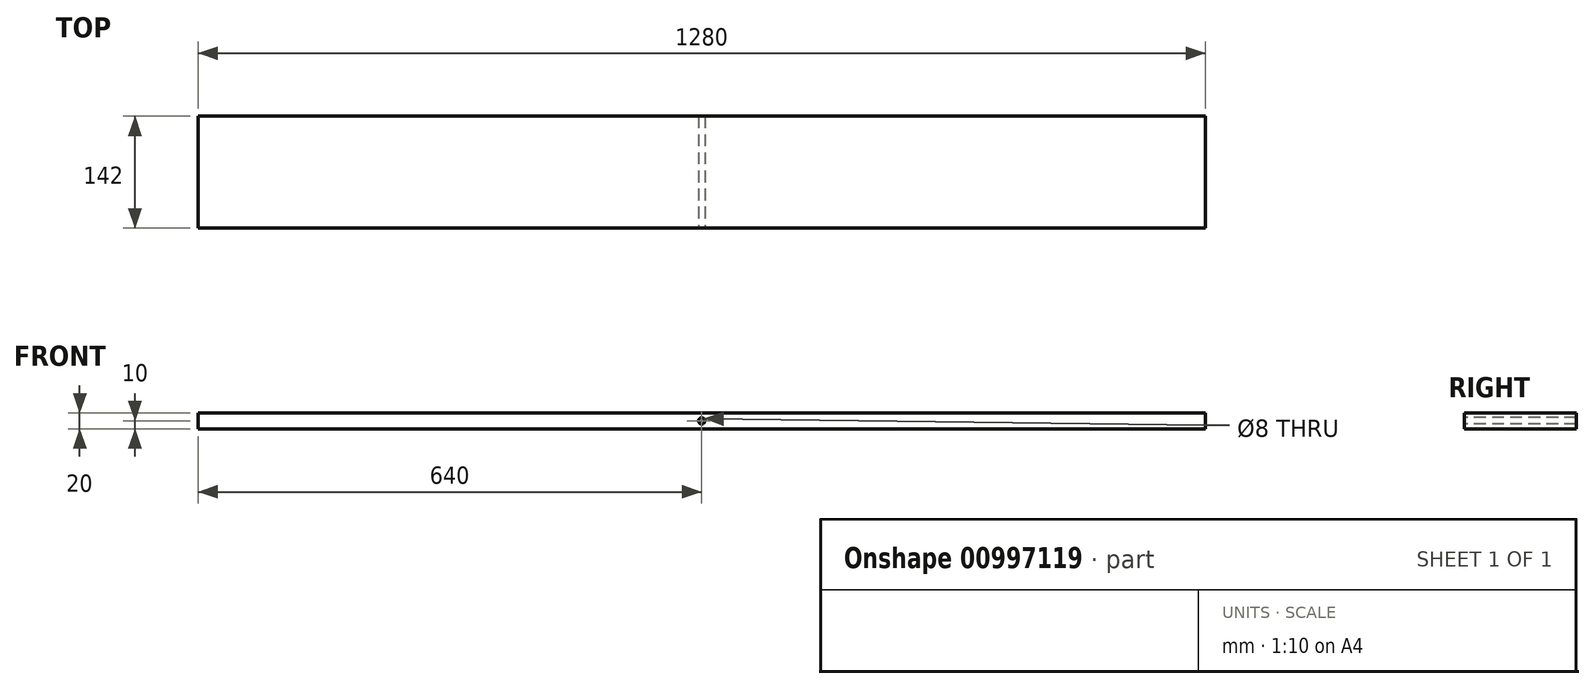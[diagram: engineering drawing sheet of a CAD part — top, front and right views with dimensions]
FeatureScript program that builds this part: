
annotation { "Feature Type Name" : "Feature", "Feature Type Description" : "" }
export const myFeature = defineFeature(function(context is Context, id is Id, definition is map)
    precondition{}
    {
        {
            var Q0;
            Q0=qCreatedBy(makeId("Top.planeOp"),FACE);
            var sketch = newSketch(context, id + "F0", { "sketchPlane" : qUnion([Q0])});
            skLineSegment(sketch, "E0.bottom", {"start": v(640, 71) * mm, "end": v(-640, 71) * mm});
            skLineSegment(sketch, "E0.top", {"start": v(640, -71) * mm, "end": v(-640, -71) * mm});
            skLineSegment(sketch, "E0.left", {"start": v(640, 71) * mm, "end": v(640, -71) * mm});
            skLineSegment(sketch, "E0.right", {"start": v(-640, 71) * mm, "end": v(-640, -71) * mm});
            skPoint(sketch, "E0.middle", {"position": v(0, 0) * mm});
            skSolve(sketch);
        }
        {
            var Q0;
            Q0=qSketchRegion(id+"F0",true);
            extrude(context, id + "F1", {"entities" : qUnion([Q0]), "endBound" : BoundingType.SYMMETRIC, "depth" : 20 * mm, "offsetDistance" : 25 * mm});
        }
        {
            var Q0;
            Q0=makeQuery(id+"F1.opExtrude","SWEPT_FACE",FACE,{"disambiguationData":[OSD([sQuery(id+"F0.wireOp",EDGE,"E0.top")])]});
            var sketch = newSketch(context, id + "F2", { "sketchPlane" : qUnion([Q0])});
            skPoint(sketch, "E1", {"position": v(0, 0) * mm});
            skSolve(sketch);
        }
        {
            var Q0;
            Q0=sQuery(id+"F2.wireOp",VERTEX,"E1");
            var Q1;
            Q1=makeQuery(id+"F1.opExtrude","SWEPT_BODY",BODY,{"disambiguationData":[OSD([sQuery(id+"F0.wireOp",EDGE,"E0.bottom"),sQuery(id+"F0.wireOp",EDGE,"E0.top"),sQuery(id+"F0.wireOp",EDGE,"E0.left"),sQuery(id+"F0.wireOp",EDGE,"E0.right")])]});
            hole(context, id + "F3", {"style" : HoleStyle.SIMPLE, "endStyle" : HoleEndStyle.THROUGH, "holeDiameter" : 8 * mm, "majorDiameter" : 5 * mm, "isTappedThrough" : true, "tappedDepth" : 12 * mm, "tapClearance" : 3, "locations" : qUnion([Q0]), "scope" : qUnion([Q1])});
        }
    });
